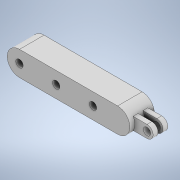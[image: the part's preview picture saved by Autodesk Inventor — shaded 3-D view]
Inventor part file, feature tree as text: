
AUTODESK INVENTOR PART (.ipt)
format: ipt  version: 2022 (Build 260153000, 153)  size: 144,896 bytes
history: native  units: mm
features: plane x3, extrude x2, sketch x2, mirror x1
ambient origin geometry x8: Origin, YZ Plane, XZ Plane, XY Plane, X Axis, Y Axis, Z Axis, Center Point
bodies: Solid1 (feature_tree)
feature tree (8):
  extrude  "Extrusion1"  Depth=20.0mm
  plane  "Work Plane5"
  extrude  "Extrusion4"  Depth=20.0mm
  plane  "Work Plane6"
  mirror  "Mirror2"
  sketch  "Sketch1"  dims[d0=20.0mm d3=6.0mm]
  plane  "Work Plane4"
  sketch  "Sketch4"  dims[d5=6.0mm d6=20.0mm d7=0.0mm d18=10.0mm d19=20.0mm d20=2.0mm d21=6.0mm d22=4.0mm d23=0.0mm d25=6.0mm d29=30.0mm d31=30.0mm]
